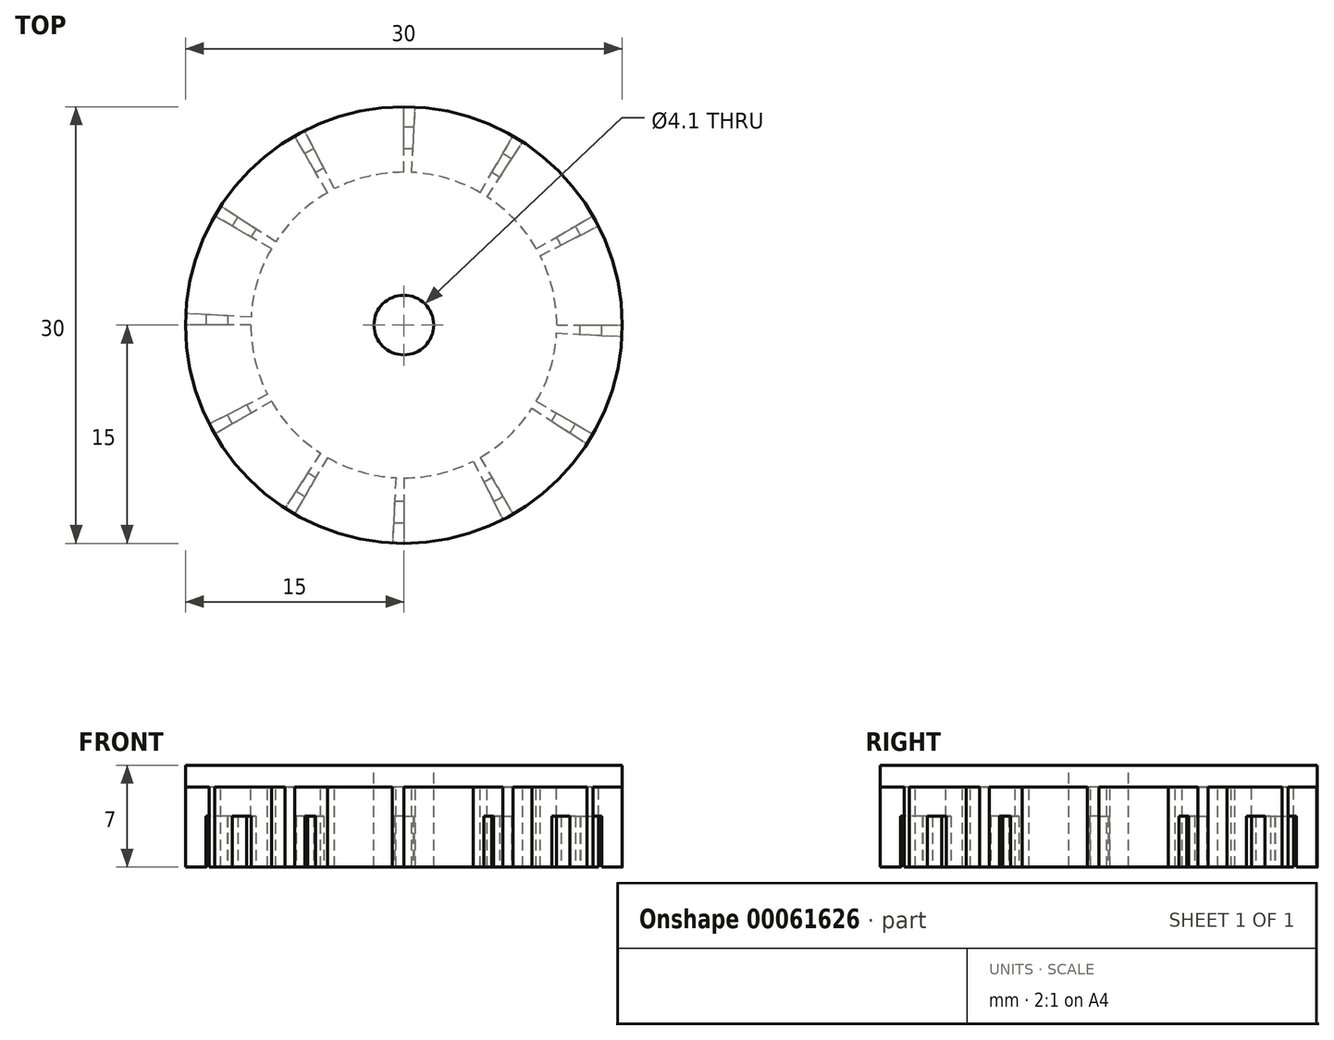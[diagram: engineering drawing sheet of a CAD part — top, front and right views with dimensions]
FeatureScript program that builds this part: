
annotation { "Feature Type Name" : "Feature", "Feature Type Description" : "" }
export const myFeature = defineFeature(function(context is Context, id is Id, definition is map)
    precondition{}
    {
        {
            var Q0;
            Q0=qCreatedBy(makeId("Top.planeOp"),FACE);
            var sketch = newSketch(context, id + "F0", { "sketchPlane" : qUnion([Q0])});
            skArc(sketch, "E0", {"start": v(12.58, -8.17) * mm, "mid": v(12.79, -7.84) * mm, "end": v(13, -7.5) * mm});
            skLineSegment(sketch, "E1", {"start": v(5.25, 9.1) * mm, "end": v(7.5, 13) * mm});
            skLineSegment(sketch, "E2.1.0", {"start": v(0, 10.5) * mm, "end": v(0, 15) * mm});
            skLineSegment(sketch, "E2.2.0", {"start": v(-5.25, 9.1) * mm, "end": v(-7.5, 13) * mm});
            skLineSegment(sketch, "E2.3.0", {"start": v(-9.1, 5.25) * mm, "end": v(-13, 7.5) * mm});
            skLineSegment(sketch, "E2.4.0", {"start": v(-10.5, 0) * mm, "end": v(-15, 0) * mm});
            skLineSegment(sketch, "E2.5.0", {"start": v(-9.1, -5.25) * mm, "end": v(-13, -7.5) * mm});
            skLineSegment(sketch, "E2.6.0", {"start": v(-5.25, -9.1) * mm, "end": v(-7.5, -13) * mm});
            skLineSegment(sketch, "E2.7.0", {"start": v(0, -10.5) * mm, "end": v(0, -15) * mm});
            skLineSegment(sketch, "E2.8.0", {"start": v(5.25, -9.1) * mm, "end": v(7.5, -13) * mm});
            skLineSegment(sketch, "E2.9.0", {"start": v(9.1, -5.25) * mm, "end": v(13, -7.5) * mm});
            skLineSegment(sketch, "E2.10.0", {"start": v(10.5, 0) * mm, "end": v(15, 0) * mm});
            skLineSegment(sketch, "E2.11.0", {"start": v(9.1, 5.25) * mm, "end": v(13, 7.5) * mm});
            skLineSegment(sketch, "E3", {"start": v(9.36, 4.77) * mm, "end": v(13.37, 6.8) * mm});
            skLineSegment(sketch, "E4.1.0", {"start": v(5.72, 8.8) * mm, "end": v(8.17, 12.58) * mm});
            skLineSegment(sketch, "E4.2.0", {"start": v(0.55, 10.49) * mm, "end": v(0.79, 14.98) * mm});
            skLineSegment(sketch, "E4.3.0", {"start": v(-4.77, 9.36) * mm, "end": v(-6.8, 13.37) * mm});
            skLineSegment(sketch, "E4.4.0", {"start": v(-8.8, 5.72) * mm, "end": v(-12.58, 8.17) * mm});
            skLineSegment(sketch, "E4.5.0", {"start": v(-10.49, 0.55) * mm, "end": v(-14.98, 0.79) * mm});
            skLineSegment(sketch, "E4.6.0", {"start": v(-9.36, -4.77) * mm, "end": v(-13.37, -6.8) * mm});
            skLineSegment(sketch, "E4.7.0", {"start": v(-5.72, -8.8) * mm, "end": v(-8.17, -12.58) * mm});
            skLineSegment(sketch, "E4.8.0", {"start": v(-0.55, -10.49) * mm, "end": v(-0.79, -14.98) * mm});
            skLineSegment(sketch, "E4.9.0", {"start": v(4.77, -9.36) * mm, "end": v(6.8, -13.37) * mm});
            skLineSegment(sketch, "E4.10.0", {"start": v(8.8, -5.72) * mm, "end": v(12.58, -8.17) * mm});
            skLineSegment(sketch, "E4.11.0", {"start": v(10.49, -0.55) * mm, "end": v(14.98, -0.79) * mm});
            skArc(sketch, "E5", {"start": v(9.1, -5.25) * mm, "mid": v(10.07, -2.98) * mm, "end": v(10.49, -0.55) * mm});
            skArc(sketch, "E6.trimOffspring", {"start": v(14.98, -0.79) * mm, "mid": v(15, -0.4) * mm, "end": v(15, 0) * mm});
            skArc(sketch, "E7.trimOffspring", {"start": v(13.37, 6.8) * mm, "mid": v(13.18, 7.16) * mm, "end": v(13, 7.5) * mm});
            skArc(sketch, "E8.trimOffspring", {"start": v(8.17, 12.58) * mm, "mid": v(7.84, 12.79) * mm, "end": v(7.5, 13) * mm});
            skArc(sketch, "E9.trimOffspring", {"start": v(0.79, 14.98) * mm, "mid": v(0.4, 15) * mm, "end": v(0, 15) * mm});
            skArc(sketch, "E10.trimOffspring", {"start": v(-6.8, 13.37) * mm, "mid": v(-7.16, 13.18) * mm, "end": v(-7.5, 13) * mm});
            skArc(sketch, "E11.trimOffspring", {"start": v(-12.58, 8.17) * mm, "mid": v(-12.79, 7.84) * mm, "end": v(-13, 7.5) * mm});
            skArc(sketch, "E12.trimOffspring", {"start": v(-14.98, 0.79) * mm, "mid": v(-15, 0.4) * mm, "end": v(-15, 0) * mm});
            skArc(sketch, "E13.trimOffspring", {"start": v(-13.37, -6.8) * mm, "mid": v(-13.18, -7.16) * mm, "end": v(-13, -7.5) * mm});
            skArc(sketch, "E14.trimOffspring", {"start": v(-8.17, -12.58) * mm, "mid": v(-7.84, -12.79) * mm, "end": v(-7.5, -13) * mm});
            skArc(sketch, "E15.trimOffspring", {"start": v(-0.79, -14.98) * mm, "mid": v(-0.4, -15) * mm, "end": v(0, -15) * mm});
            skArc(sketch, "E16.trimOffspring", {"start": v(6.8, -13.37) * mm, "mid": v(7.16, -13.18) * mm, "end": v(7.5, -13) * mm});
            skArc(sketch, "E17.trimOffspring", {"start": v(10.5, 0) * mm, "mid": v(10.2, 2.45) * mm, "end": v(9.36, 4.77) * mm});
            skArc(sketch, "E18.trimOffspring", {"start": v(9.1, 5.25) * mm, "mid": v(7.62, 7.23) * mm, "end": v(5.72, 8.8) * mm});
            skArc(sketch, "E19.trimOffspring", {"start": v(5.25, 9.1) * mm, "mid": v(2.98, 10.07) * mm, "end": v(0.55, 10.49) * mm});
            skArc(sketch, "E20.trimOffspring", {"start": v(0, 10.5) * mm, "mid": v(-2.45, 10.2) * mm, "end": v(-4.77, 9.36) * mm});
            skArc(sketch, "E21.trimOffspring", {"start": v(-5.25, 9.1) * mm, "mid": v(-7.23, 7.62) * mm, "end": v(-8.8, 5.72) * mm});
            skArc(sketch, "E22.trimOffspring", {"start": v(-9.1, 5.25) * mm, "mid": v(-10.07, 2.98) * mm, "end": v(-10.49, 0.55) * mm});
            skArc(sketch, "E23.trimOffspring", {"start": v(-10.5, 0) * mm, "mid": v(-10.2, -2.45) * mm, "end": v(-9.36, -4.77) * mm});
            skArc(sketch, "E24.trimOffspring", {"start": v(-9.1, -5.25) * mm, "mid": v(-7.62, -7.23) * mm, "end": v(-5.72, -8.8) * mm});
            skArc(sketch, "E25.trimOffspring", {"start": v(-5.25, -9.1) * mm, "mid": v(-2.98, -10.07) * mm, "end": v(-0.55, -10.49) * mm});
            skArc(sketch, "E26.trimOffspring", {"start": v(0, -10.5) * mm, "mid": v(2.45, -10.2) * mm, "end": v(4.77, -9.36) * mm});
            skArc(sketch, "E27.trimOffspring", {"start": v(5.25, -9.1) * mm, "mid": v(7.23, -7.62) * mm, "end": v(8.8, -5.72) * mm});
            skSolve(sketch);
        }
        {
            var Q0;
            Q0=makeQuery(id+"F0.imprint","IMPRINT",FACE,{"disambiguationData":[TD([[makeQuery(id+"F0.imprint","IMPRINT",EDGE,{"derivedFrom":sQuery(id+"F0.wireOp",EDGE,"E0")}),1.0]])]});
            extrude(context, id + "F1", {"entities" : qUnion([Q0]), "oppositeDirection" : true, "depth" : 5.5 * mm});
        }
        {
            var Q0;
            Q0=makeQuery(id+"F1.opExtrude","CAP_FACE",FACE,{"disambiguationData":[OSD([sQuery(id+"F0.wireOp",EDGE,"E0"),sQuery(id+"F0.wireOp",EDGE,"E1"),sQuery(id+"F0.wireOp",EDGE,"E2.1.0"),sQuery(id+"F0.wireOp",EDGE,"E2.2.0"),sQuery(id+"F0.wireOp",EDGE,"E2.3.0"),sQuery(id+"F0.wireOp",EDGE,"E2.4.0"),sQuery(id+"F0.wireOp",EDGE,"E2.5.0"),sQuery(id+"F0.wireOp",EDGE,"E2.6.0"),sQuery(id+"F0.wireOp",EDGE,"E2.7.0"),sQuery(id+"F0.wireOp",EDGE,"E2.8.0"),sQuery(id+"F0.wireOp",EDGE,"E2.9.0"),sQuery(id+"F0.wireOp",EDGE,"E2.10.0"),sQuery(id+"F0.wireOp",EDGE,"E2.11.0"),sQuery(id+"F0.wireOp",EDGE,"E3"),sQuery(id+"F0.wireOp",EDGE,"E4.1.0"),sQuery(id+"F0.wireOp",EDGE,"E4.2.0"),sQuery(id+"F0.wireOp",EDGE,"E4.3.0"),sQuery(id+"F0.wireOp",EDGE,"E4.4.0"),sQuery(id+"F0.wireOp",EDGE,"E4.5.0"),sQuery(id+"F0.wireOp",EDGE,"E4.6.0"),sQuery(id+"F0.wireOp",EDGE,"E4.7.0"),sQuery(id+"F0.wireOp",EDGE,"E4.8.0"),sQuery(id+"F0.wireOp",EDGE,"E4.9.0"),sQuery(id+"F0.wireOp",EDGE,"E4.10.0"),sQuery(id+"F0.wireOp",EDGE,"E4.11.0"),sQuery(id+"F0.wireOp",EDGE,"E5"),sQuery(id+"F0.wireOp",EDGE,"E6.trimOffspring"),sQuery(id+"F0.wireOp",EDGE,"E7.trimOffspring"),sQuery(id+"F0.wireOp",EDGE,"E8.trimOffspring"),sQuery(id+"F0.wireOp",EDGE,"E9.trimOffspring"),sQuery(id+"F0.wireOp",EDGE,"E10.trimOffspring"),sQuery(id+"F0.wireOp",EDGE,"E11.trimOffspring"),sQuery(id+"F0.wireOp",EDGE,"E12.trimOffspring"),sQuery(id+"F0.wireOp",EDGE,"E13.trimOffspring"),sQuery(id+"F0.wireOp",EDGE,"E14.trimOffspring"),sQuery(id+"F0.wireOp",EDGE,"E15.trimOffspring"),sQuery(id+"F0.wireOp",EDGE,"E16.trimOffspring"),sQuery(id+"F0.wireOp",EDGE,"E17.trimOffspring"),sQuery(id+"F0.wireOp",EDGE,"E18.trimOffspring"),sQuery(id+"F0.wireOp",EDGE,"E19.trimOffspring"),sQuery(id+"F0.wireOp",EDGE,"E20.trimOffspring"),sQuery(id+"F0.wireOp",EDGE,"E21.trimOffspring"),sQuery(id+"F0.wireOp",EDGE,"E22.trimOffspring"),sQuery(id+"F0.wireOp",EDGE,"E23.trimOffspring"),sQuery(id+"F0.wireOp",EDGE,"E24.trimOffspring"),sQuery(id+"F0.wireOp",EDGE,"E25.trimOffspring"),sQuery(id+"F0.wireOp",EDGE,"E26.trimOffspring"),sQuery(id+"F0.wireOp",EDGE,"E27.trimOffspring")])],"isStart":true});
            var sketch = newSketch(context, id + "F2", { "sketchPlane" : qUnion([Q0])});
            skCircle(sketch, "E28", {"center": v(0, 0) * mm, "radius": 15 * mm});
            skSolve(sketch);
        }
        {
            var Q0;
            Q0 = qSketchRegion(id + "F2", true);
            extrude(context, id + "F3", {"entities" : qUnion([Q0]), "operationType" : NewBodyOperationType.ADD, "depth" : 1.5 * mm});
        }
        {
            var Q0;
            Q0=makeQuery(id+"F1.opExtrude","CAP_FACE",FACE,{"disambiguationData":[OSD([sQuery(id+"F0.wireOp",EDGE,"E0"),sQuery(id+"F0.wireOp",EDGE,"E1"),sQuery(id+"F0.wireOp",EDGE,"E2.1.0"),sQuery(id+"F0.wireOp",EDGE,"E2.2.0"),sQuery(id+"F0.wireOp",EDGE,"E2.3.0"),sQuery(id+"F0.wireOp",EDGE,"E2.4.0"),sQuery(id+"F0.wireOp",EDGE,"E2.5.0"),sQuery(id+"F0.wireOp",EDGE,"E2.6.0"),sQuery(id+"F0.wireOp",EDGE,"E2.7.0"),sQuery(id+"F0.wireOp",EDGE,"E2.8.0"),sQuery(id+"F0.wireOp",EDGE,"E2.9.0"),sQuery(id+"F0.wireOp",EDGE,"E2.10.0"),sQuery(id+"F0.wireOp",EDGE,"E2.11.0"),sQuery(id+"F0.wireOp",EDGE,"E3"),sQuery(id+"F0.wireOp",EDGE,"E4.1.0"),sQuery(id+"F0.wireOp",EDGE,"E4.2.0"),sQuery(id+"F0.wireOp",EDGE,"E4.3.0"),sQuery(id+"F0.wireOp",EDGE,"E4.4.0"),sQuery(id+"F0.wireOp",EDGE,"E4.5.0"),sQuery(id+"F0.wireOp",EDGE,"E4.6.0"),sQuery(id+"F0.wireOp",EDGE,"E4.7.0"),sQuery(id+"F0.wireOp",EDGE,"E4.8.0"),sQuery(id+"F0.wireOp",EDGE,"E4.9.0"),sQuery(id+"F0.wireOp",EDGE,"E4.10.0"),sQuery(id+"F0.wireOp",EDGE,"E4.11.0"),sQuery(id+"F0.wireOp",EDGE,"E5"),sQuery(id+"F0.wireOp",EDGE,"E6.trimOffspring"),sQuery(id+"F0.wireOp",EDGE,"E7.trimOffspring"),sQuery(id+"F0.wireOp",EDGE,"E8.trimOffspring"),sQuery(id+"F0.wireOp",EDGE,"E9.trimOffspring"),sQuery(id+"F0.wireOp",EDGE,"E10.trimOffspring"),sQuery(id+"F0.wireOp",EDGE,"E11.trimOffspring"),sQuery(id+"F0.wireOp",EDGE,"E12.trimOffspring"),sQuery(id+"F0.wireOp",EDGE,"E13.trimOffspring"),sQuery(id+"F0.wireOp",EDGE,"E14.trimOffspring"),sQuery(id+"F0.wireOp",EDGE,"E15.trimOffspring"),sQuery(id+"F0.wireOp",EDGE,"E16.trimOffspring"),sQuery(id+"F0.wireOp",EDGE,"E17.trimOffspring"),sQuery(id+"F0.wireOp",EDGE,"E18.trimOffspring"),sQuery(id+"F0.wireOp",EDGE,"E19.trimOffspring"),sQuery(id+"F0.wireOp",EDGE,"E20.trimOffspring"),sQuery(id+"F0.wireOp",EDGE,"E21.trimOffspring"),sQuery(id+"F0.wireOp",EDGE,"E22.trimOffspring"),sQuery(id+"F0.wireOp",EDGE,"E23.trimOffspring"),sQuery(id+"F0.wireOp",EDGE,"E24.trimOffspring"),sQuery(id+"F0.wireOp",EDGE,"E25.trimOffspring"),sQuery(id+"F0.wireOp",EDGE,"E26.trimOffspring"),sQuery(id+"F0.wireOp",EDGE,"E27.trimOffspring")])],"isStart":false});
            var sketch = newSketch(context, id + "F4", { "sketchPlane" : qUnion([Q0])});
            skCircle(sketch, "E29", {"center": v(0, 0) * mm, "radius": 12.1 * mm});
            skCircle(sketch, "E30", {"center": v(0, 0) * mm, "radius": 13.6 * mm});
            skSolve(sketch);
        }
        {
            var Q0;
            Q0 = qSketchRegion(id + "F4", true);
            extrude(context, id + "F5", {"entities" : qUnion([Q0]), "operationType" : NewBodyOperationType.REMOVE, "oppositeDirection" : true, "depth" : 3.5 * mm});
        }
        {
            var Q0;
            Q0=makeQuery(id+"F3.opExtrude","CAP_FACE",FACE,{"disambiguationData":[OSD([sQuery(id+"F2.wireOp",EDGE,"E28")])],"isStart":false});
            var sketch = newSketch(context, id + "F6", { "sketchPlane" : qUnion([Q0])});
            skCircle(sketch, "E31", {"center": v(0, 0) * mm, "radius": 2.05 * mm});
            skSolve(sketch);
        }
        {
            var Q0;
            Q0 = qSketchRegion(id + "F6", true);
            extrude(context, id + "F7", {"entities" : qUnion([Q0]), "operationType" : NewBodyOperationType.REMOVE, "endBound" : BoundingType.THROUGH_ALL, "oppositeDirection" : true, "depth" : 25 * mm});
        }
    });
